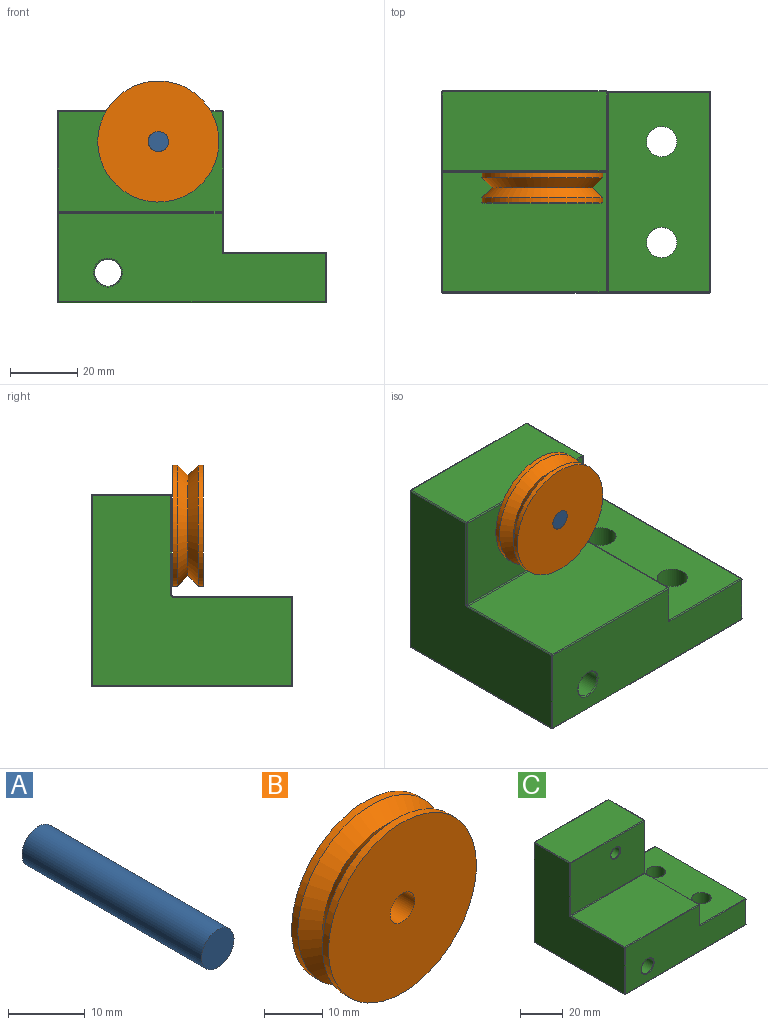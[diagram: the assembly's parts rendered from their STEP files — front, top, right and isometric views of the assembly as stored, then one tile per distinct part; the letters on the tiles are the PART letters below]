
ASSEMBLY  parts=3 mates=2
PART A: 3 faces, bbox 6x33x6 mm
  f0: cylinder r=3mm len=33mm, axis (0,1,0), area 622mm2, adj f1,f2
  f1: plane 6x6mm, normal (0,-1,0), area 28.3mm2, adj f0
  f2: plane 6x6mm, normal (0,1,0), area 28.3mm2, adj f0
PART B: 7 faces, bbox 36x9x36 mm
  f0: cone r=15mm half-angle=45deg, axis (0,-1,0), area 439.8mm2, adj f1,f3
  f1: cylinder r=18mm len=36mm, axis (0,1,0), area 169.6mm2, adj f0,f2
  f2: plane 36x36mm, normal (0,-1,0), area 989.6mm2, adj f1,f6
  f3: cone r=15mm half-angle=45deg, axis (0,1,0), area 439.8mm2, adj f0,f4
  f4: cylinder r=18mm len=36mm, axis (0,-1,0), area 169.6mm2, adj f3,f5
  f5: plane 36x36mm, normal (0,1,0), area 989.6mm2, adj f4,f6
  f6: cylinder r=3mm len=9mm, axis (0,1,0), area 169.6mm2, adj f2,f5
PART C: 68 faces, bbox 80x60x57.2 mm
  f0: plane 79.4x26.4mm, normal (0,-1,0), area 1668.9mm2, adj f24,f42,f43,f54,f55,f59,f63,f64
  f1: cylinder r=7.95mm len=19.2mm, axis (0,0,-1), area 855.1mm2, adj f17,f18,f19,f25
  f2: plane 59.4x41.55mm, normal (1,0,0), area 1382.7mm2, adj f39,f52,f53,f62,f63,f65,f67
  f3: plane 79.4x56.55mm, normal (0,1,0), area 3100.9mm2, adj f22,f23,f29,f31,f32,f38,f39,f40
  f4: plane 59.4x56.55mm, normal (-1,0,0), area 2273.7mm2, adj f32,f37,f44,f50,f55,f56,f57
  f5: plane 48.63x29.55mm, normal (0,-1,0), area 1402.8mm2, adj f21,f50,f51,f61,f62
  f6: plane 48.63x23.4mm, normal (0,0,1), area 1137.9mm2, adj f37,f38,f51,f52
  f7: plane 59.4x30.17mm, normal (0,0,1), area 1664.9mm2, adj f11,f14,f40,f41,f53,f54
  f8: plane 59.4x14.4mm, normal (1,0,0), area 855.4mm2, adj f29,f30,f41,f42
  f9: plane 79.4x59.4mm, normal (0,0,-1), area 4156.1mm2, adj f25,f26,f27,f30,f31,f43,f44
  f10: plane 48.63x35.4mm, normal (0,0,1), area 1721.5mm2, adj f56,f61,f64,f67
  f11: cylinder r=4.5mm len=9mm, axis (0,0,-1), area 197.9mm2, adj f7,f12
  f12: plane 14.25x14.25mm, normal (0,0,-1), area 95.9mm2, adj f11,f13
  f13: cylinder r=7.12mm len=14.25mm, axis (0,0,-1), area 344.7mm2, adj f12,f26
  f14: cylinder r=4.5mm len=9mm, axis (0,0,-1), area 197.9mm2, adj f7,f15
  f15: plane 14.25x14.25mm, normal (0,0,-1), area 95.9mm2, adj f14,f16
  f16: cylinder r=7.12mm len=14.25mm, axis (0,0,-1), area 344.7mm2, adj f15,f27
  f17: cone r=0mm half-angle=59deg, axis (0,0,-1), area 231.6mm2, adj f1
  f18: cylinder r=4mm len=22.89mm, axis (0,-1,0), area 561.4mm2, adj f1,f24
  f19: cylinder r=4mm len=22.77mm, axis (0,-1,0), area 558.5mm2, adj f1,f23
  f20: cylinder r=3mm len=23.4mm, axis (0,1,0), area 441.1mm2, adj f21,f22
  f21: torus R=3.3mm, axis (0,1,0), area 9.2mm2, adj f5,f20
  f22: torus R=3.3mm, axis (0,1,0), area 9.2mm2, adj f3,f20
  f23: torus R=4.3mm, axis (0,1,0), area 12.2mm2, adj f3,f19
  f24: torus R=4.3mm, axis (0,1,0), area 12.2mm2, adj f0,f18
  f25: torus R=8.25mm, axis (0,0,-1), area 23.9mm2, adj f1,f9
  f26: torus R=7.42mm, axis (0,0,-1), area 21.4mm2, adj f9,f13
  f27: torus R=7.42mm, axis (0,0,-1), area 21.4mm2, adj f9,f16
  f28: sphere r=0.3mm, area 0.1mm2, adj f29,f30,f31
  f29: cylinder r=0.3mm len=14.4mm, axis (0,0,1), area 6.8mm2, adj f3,f8,f28,f34
  f30: cylinder r=0.3mm len=59.4mm, axis (0,1,0), area 28mm2, adj f8,f9,f28,f35
  f31: cylinder r=0.3mm len=79.4mm, axis (-1,0,0), area 37.4mm2, adj f3,f9,f28,f36
  f32: cylinder r=0.3mm len=56.55mm, axis (0,0,1), area 26.6mm2, adj f3,f4,f33,f36
  f33: sphere r=0.3mm, area 0.1mm2, adj f32,f37,f38
  f34: sphere r=0.3mm, area 0.1mm2, adj f29,f40,f41
  f35: sphere r=0.3mm, area 0.1mm2, adj f30,f42,f43
  f36: sphere r=0.3mm, area 0.1mm2, adj f31,f32,f44
  f37: cylinder r=0.3mm len=23.4mm, axis (0,1,0), area 11mm2, adj f4,f6,f33,f45
  f38: cylinder r=0.3mm len=48.63mm, axis (1,0,0), area 22.9mm2, adj f3,f6,f33,f46
  f39: cylinder r=0.3mm len=41.55mm, axis (0,0,-1), area 19.6mm2, adj f2,f3,f46,f47
  f40: cylinder r=0.3mm len=30.17mm, axis (1,0,0), area 14.2mm2, adj f3,f7,f34,f47
  f41: cylinder r=0.3mm len=59.4mm, axis (0,-1,0), area 28mm2, adj f7,f8,f34,f48
  f42: cylinder r=0.3mm len=14.4mm, axis (0,0,-1), area 6.8mm2, adj f0,f8,f35,f48
  f43: cylinder r=0.3mm len=79.4mm, axis (1,0,0), area 37.4mm2, adj f0,f9,f35,f49
  f44: cylinder r=0.3mm len=59.4mm, axis (0,-1,0), area 28mm2, adj f4,f9,f36,f49
  f45: sphere r=0.3mm, area 0.1mm2, adj f37,f50,f51
  f46: sphere r=0.3mm, area 0.1mm2, adj f38,f39,f52
  f47: torus R=0.6mm, axis (0,1,0), area 0.3mm2, adj f3,f39,f40,f53
  f48: sphere r=0.3mm, area 0.1mm2, adj f41,f42,f54
  f49: sphere r=0.3mm, area 0.1mm2, adj f43,f44,f55
  f50: cylinder r=0.3mm len=29.55mm, axis (0,0,-1), area 13.9mm2, adj f4,f5,f45,f57
  f51: cylinder r=0.3mm len=48.63mm, axis (-1,0,0), area 22.9mm2, adj f5,f6,f45,f58
  f52: cylinder r=0.3mm len=23.4mm, axis (0,-1,0), area 11mm2, adj f2,f6,f46,f58
  f53: cylinder r=0.3mm len=59.4mm, axis (0,-1,0), area 28mm2, adj f2,f7,f47,f59
  f54: cylinder r=0.3mm len=30.17mm, axis (-1,0,0), area 14.2mm2, adj f0,f7,f48,f59
  f55: cylinder r=0.3mm len=26.4mm, axis (0,0,1), area 12.4mm2, adj f0,f4,f49,f60
  f56: cylinder r=0.3mm len=35.4mm, axis (0,-1,0), area 16.7mm2, adj f4,f10,f57,f60
  f57: torus R=0.6mm, axis (1,0,0), area 0.3mm2, adj f4,f50,f56,f61
  f58: sphere r=0.3mm, area 0.1mm2, adj f51,f52,f62
  f59: torus R=0.6mm, axis (0,1,0), area 0.3mm2, adj f0,f53,f54,f63
  f60: sphere r=0.3mm, area 0.1mm2, adj f55,f56,f64
  f61: cylinder r=0.3mm len=48.63mm, axis (1,0,0), area 22.9mm2, adj f5,f10,f57,f65
  f62: cylinder r=0.3mm len=29.55mm, axis (0,0,1), area 13.9mm2, adj f2,f5,f58,f65
  f63: cylinder r=0.3mm len=11.4mm, axis (0,0,1), area 5.4mm2, adj f0,f2,f59,f66
  f64: cylinder r=0.3mm len=48.63mm, axis (1,0,0), area 22.9mm2, adj f0,f10,f60,f66
  f65: torus R=0.6mm, axis (1,0,0), area 0.3mm2, adj f2,f61,f62,f67
  f66: sphere r=0.3mm, area 0.1mm2, adj f63,f64,f67
  f67: cylinder r=0.3mm len=35.4mm, axis (0,-1,0), area 16.7mm2, adj f2,f10,f65,f66
PLACE A rot(axis=(1,0,0),180deg) t=(-297.29,-96.54,-9.23)mm
PLACE B rot(axis=(0,-1,0),90deg) t=(-264.29,-14.04,310.77)mm
PLACE C t=(22.71,-18.24,-42.23)mm
MATE pin_slot A.f0 <-> C.f20  axis (0,1,0) through (-297.29,-63.54,-9.23)mm
MATE revolute B.f0 <-> A.f0  axis (0,-1,0) through (-297.29,-96.54,-9.23)mm
